# Revit family: Water_Boiler-Navien-NFB-Condensing-NFB-H
name_source: partatom
category: Mechanical Equipment
units: mm (PartAtom-declared; Revit-internal decimal feet)

## family parameters
Cut with Voids When Loaded = No
Host = Face
OmniClass Number = 23.65.35.11
OmniClass Title = Supply Water Heaters
Part Type = Normal
Room Calculation Point = No
Round Connector Dimension = Use Diameter
Shared = No

## types (2) — shared parameters
2" Exhaust/Intake = No
3" Exhaust/Intake = Yes
Apparent Load = 0 VA
Assembly Code = D3010500
Certifications = Energy Star | AHRI | CSA | ASME
Cold Water Inlet = 1"
Default Elevation = 4' - 0"
Depth = 1' - 5 5/16"
Description = NFB-H High Capacity High-Efficiency Condensing Fire Tube Boiler
Exhaust = 3"
Finish = Metal - Navien - White
Flow Rate = 0 GPM
Frequency = 60 Hz
Gas Inlet = 1"
Height = 2' - 3 19/32"
Hot Water Outlet = 1"
Ignition = Electronic ignition
Installation Type = Indoor Wall-Hung
Intake = 3"
Keynote = 22 33 00.A1
Manufacturer = Navien, Inc.
Manufacturer Fax Number = (949) 420-0430
Natural Gas Supply Pressure = 3.5" to 10.5" WC
Number of Poles = 1
Phase = 1
Power Factor = 1
Product Documentation Link = https://www.navieninc.com
Product Name = NFB-H Series Condensing Boiler
Product Page URL = https://www.navieninc.com
Propane Gas Supply Pressure = 8.0" to 13.5" WC
URL = https://www.navieninc.com
Venting = PVC, CPVC, PP | Size (3in) | Length (150 ft)
Venting Type = Forced draft direct vent
Version = 2019 - v1.0.a
Voltage = 120 V
Warranty = https://www.navieninc.com
Warranty Note = Heat Exchangers: 15 years limited warranty (Residential), 10 years (Commercial) | Parts: 5 years (Residential), 3 years (Commercial) | Labor: 1 year (Residential), 1 year (Commercial)
Water Pressure = 6-80 psi
Weight = 121.00 lbf
Wi-Fi Ready = NaviLink Wi-Fi Control: This add-on accessory enables access to control temperatures remotely, access usage data and receive diagnostic notifications via smartphone or tablet.
Width = 1' - 5 5/16"

## per-type parameters (varying)
| type | Heating Capacity | Heating Capacity Note | Natural Gas Manifold Pressure | Propane Gas Manifold Pressure |
| NFB-175H | 175000.0 Btu/h | 13,300-175,000(BTU/H) | -0.03"" to -0.70"" WC | -0.02"" to -0.68"" WC |
| NFB-200H | 199900.0 Btu/h | 13,300-199,900(BTU/H) | -0.03"" to -0.85"" WC | -0.02"" to -0.75"" WC |

note: column(s) folded — value = type name in every type: Model

## geometry (parser evidence)
native form markers: Sweep x5
no freeform markers — native parametric forms only
